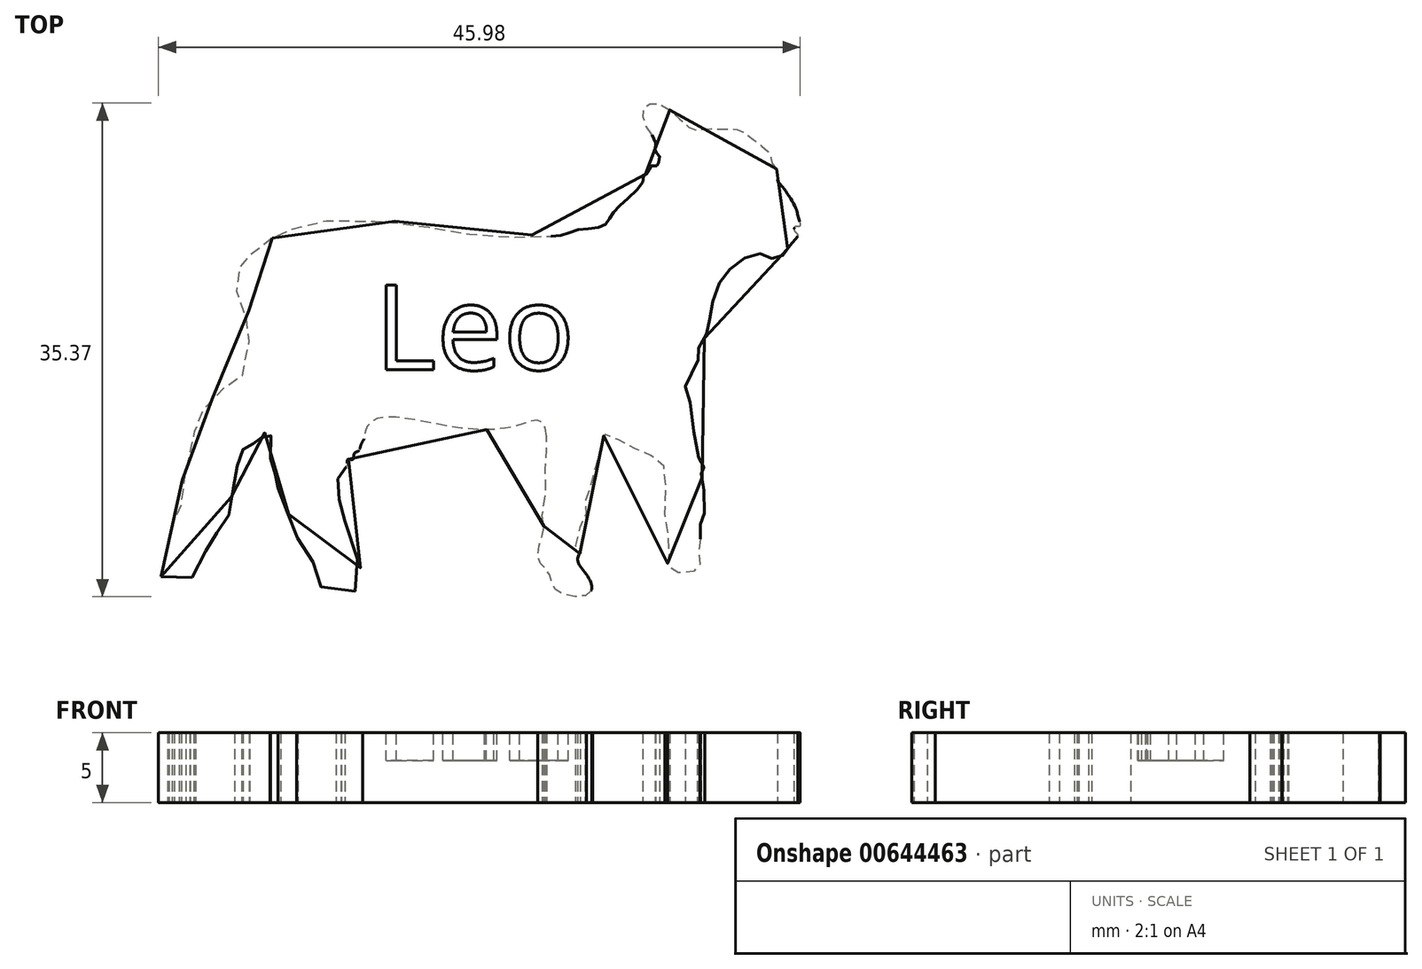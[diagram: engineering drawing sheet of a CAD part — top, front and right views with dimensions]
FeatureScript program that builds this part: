
annotation { "Feature Type Name" : "Feature", "Feature Type Description" : "" }
export const myFeature = defineFeature(function(context is Context, id is Id, definition is map)
    precondition{}
    {
        {
            var Q0;
            Q0=qCreatedBy(makeId("Top.planeOp"),FACE);
            var sketch = newSketch(context, id + "F0", { "sketchPlane" : qUnion([Q0])});
            skFitSpline(sketch, "E0", {"points": [v(-52.94, 10.3) * mm, v(-52.84, 11.68) * mm, v(-52.4, 12.88) * mm, v(-52.47, 13.1) * mm, v(-52, 13.63) * mm, v(-52.1, 13.85) * mm, v(-52.14, 14.2) * mm, v(-51.87, 14.8) * mm, v(-51.49, 15.13) * mm, v(-51.62, 15.97) * mm, v(-51.44, 17.15) * mm, v(-51.2, 17.9) * mm, v(-51.47, 18.15) * mm, v(-51.17, 18.5) * mm, v(-50.84, 19.3) * mm, v(-50.81, 20.13) * mm, v(-50.49, 20.45) * mm, v(-50.59, 21.16) * mm, v(-50.09, 21.6) * mm, v(-49.94, 22.2) * mm, v(-49.39, 22.7) * mm, v(-49.11, 23.4) * mm, v(-47.74, 24.2) * mm, v(-47.66, 24.51) * mm, v(-47.15, 24.58) * mm, v(-47.15, 25.06) * mm, v(-46.75, 25.6) * mm, v(-46.84, 27.96) * mm, v(-47.05, 28.11) * mm, v(-46.94, 28.45) * mm, v(-46.77, 28.93) * mm, v(-46.68, 29.98) * mm, v(-47.62, 30.87) * mm, v(-47.55, 31.93) * mm, v(-47.44, 32.43) * mm, v(-47.12, 32.54) * mm, v(-47.1, 33.02) * mm, v(-46.77, 33) * mm, v(-46.45, 33.46) * mm, v(-45.92, 33.69) * mm, v(-45.7, 34) * mm, v(-44.65, 34.61) * mm, v(-44.01, 34.57) * mm, v(-43.83, 35.09) * mm, v(-42.7, 35.16) * mm, v(-41.74, 35.67) * mm, v(-38.42, 35.76) * mm, v(-37.44, 35.7) * mm, v(-36.52, 35.51) * mm, v(-36.17, 35.76) * mm, v(-35.5, 35.27) * mm, v(-34.6, 35.28) * mm, v(-33.3, 35.28) * mm, v(-31.46, 34.9) * mm, v(-29.54, 34.73) * mm, v(-27.63, 34.62) * mm, v(-26.32, 34.77) * mm, v(-24.45, 34.7) * mm, v(-23.05, 35.14) * mm, v(-21.32, 35.39) * mm, v(-20.76, 36.04) * mm, v(-19.88, 37.05) * mm, v(-18.41, 38.61) * mm, v(-18.3, 39.1) * mm, v(-18, 39.24) * mm, v(-17.88, 39.7) * mm, v(-17.41, 39.73) * mm, v(-17.27, 40.02) * mm, v(-17.26, 40.52) * mm, v(-17.51, 40.66) * mm, v(-17.53, 41.39) * mm, v(-18.29, 42.78) * mm, v(-18.23, 44) * mm, v(-16.92, 44.02) * mm, v(-14.9, 42.35) * mm, v(-14.04, 42.37) * mm, v(-12.82, 42.35) * mm, v(-11.58, 42.3) * mm, v(-10.2, 41.37) * mm, v(-9.3, 40.5) * mm, v(-9.15, 39.85) * mm, v(-8.8, 39.41) * mm, v(-8.78, 38.78) * mm, v(-8.36, 38.13) * mm, v(-7.45, 36.64) * mm, v(-7.3, 36.08) * mm, v(-7.16, 35.56) * mm, v(-7.22, 35.37) * mm, v(-7.52, 35.36) * mm, v(-7.58, 35.12) * mm, v(-7.43, 34.92) * mm, v(-7.32, 34.67) * mm, v(-7.93, 33.96) * mm, v(-8.4, 33.3) * mm, v(-9.18, 33.08) * mm, v(-10.1, 33.43) * mm, v(-11.73, 32.7) * mm, v(-12.91, 31.37) * mm, v(-13.6, 29.17) * mm, v(-13.8, 27.78) * mm, v(-14.5, 26.47) * mm, v(-14.47, 25.6) * mm, v(-15.35, 24.22) * mm, v(-15.1, 23.05) * mm, v(-14.39, 18.7) * mm, v(-14.05, 18.12) * mm, v(-14.22, 17.82) * mm, v(-14.18, 17.4) * mm, v(-14.04, 14.66) * mm, v(-14.32, 14) * mm, v(-14.32, 12.55) * mm, v(-14.43, 11.53) * mm, v(-14.33, 11.07) * mm, v(-14.86, 10.65) * mm, v(-16.2, 10.65) * mm, v(-16.66, 11.18) * mm, v(-16.49, 12.1) * mm, v(-16.84, 14.86) * mm, v(-16.91, 18.19) * mm, v(-18.26, 19.14) * mm, v(-20.03, 20) * mm, v(-21.16, 20.45) * mm, v(-21.44, 19.07) * mm, v(-22.12, 17.34) * mm, v(-22.05, 16.7) * mm, v(-22.47, 16.35) * mm, v(-22.47, 15.04) * mm, v(-22.75, 14.26) * mm, v(-23.21, 12.42) * mm, v(-22.9, 12.1) * mm, v(-23.1, 11.57) * mm, v(-22.22, 10.04) * mm, v(-22.36, 9.02) * mm, v(-24.63, 9.3) * mm, v(-25.16, 10.58) * mm, v(-25.94, 11.6) * mm, v(-25.52, 13.73) * mm, v(-25.62, 14.5) * mm, v(-25.4, 16.13) * mm, v(-25.4, 17.55) * mm, v(-25.37, 18.47) * mm, v(-25.62, 21.34) * mm, v(-27.36, 21.13) * mm, v(-31.85, 20.99) * mm, v(-37.45, 21.62) * mm, v(-38.33, 20.67) * mm, v(-38.41, 20.12) * mm, v(-38.6, 19.78) * mm, v(-38.78, 19.3) * mm, v(-39.08, 19.14) * mm, v(-39.2, 18.7) * mm, v(-39.56, 18.68) * mm, v(-39.65, 18.18) * mm, v(-40.02, 17.9) * mm, v(-40.02, 17.46) * mm, v(-40.34, 17.23) * mm, v(-40.32, 16.47) * mm, v(-40.11, 15.65) * mm, v(-39.78, 14.77) * mm, v(-39.76, 14.04) * mm, v(-38.77, 11.2) * mm, v(-38.77, 9.43) * mm, v(-41.04, 9.17) * mm, v(-41.69, 10.15) * mm, v(-41.94, 11.17) * mm, v(-43.2, 12.65) * mm, v(-43.13, 13.24) * mm, v(-43.71, 14.64) * mm, v(-44.27, 15.43) * mm, v(-44.55, 16.64) * mm, v(-44.4, 16.95) * mm, v(-44.45, 17.28) * mm, v(-44.83, 17.67) * mm, v(-44.96, 18.08) * mm, v(-45.1, 18.7) * mm, v(-45.1, 18.93) * mm, v(-45.13, 19.94) * mm, v(-45.13, 20.64) * mm, v(-45.48, 20.63) * mm, v(-45.7, 20.33) * mm, v(-45.88, 20.15) * mm, v(-46.05, 20.09) * mm, v(-46.12, 19.95) * mm, v(-46.3, 19.9) * mm, v(-46.4, 19.69) * mm, v(-46.66, 19.57) * mm, v(-46.82, 19.43) * mm, v(-47.1, 19.4) * mm, v(-47.32, 19.1) * mm, v(-47.45, 18.5) * mm, v(-47.58, 17.65) * mm, v(-47.7, 16.87) * mm, v(-48, 15.55) * mm, v(-48.1, 14.61) * mm, v(-48.39, 14.04) * mm, v(-48.98, 13.39) * mm, v(-49.25, 12.6) * mm, v(-49.8, 12.05) * mm, v(-50.69, 10.46) * mm, v(-50.85, 10.07) * mm, v(-52.94, 10.3) * mm]});
            skSolve(sketch);
        }
        {
            var Q0;
            Q0=makeQuery(id+"F0.imprint","IMPRINT",FACE,{"disambiguationData":[TD([[makeQuery(id+"F0.imprint","IMPRINT",EDGE,{"derivedFrom":sQuery(id+"F0.wireOp",EDGE,"E0")}),-1.0]])]});
            extrude(context, id + "F1", {"entities" : qUnion([Q0]), "depth" : 5 * mm, "offsetDistance" : 25 * mm});
        }
        {
            var Q0;
            Q0=qCreatedBy(makeId("Top.planeOp"),FACE);
            var sketch = newSketch(context, id + "F2", { "sketchPlane" : qUnion([Q0])});
            skText(sketch, "E1", { "text": "Lamb", "fontName": "OpenSans-Regular.ttf"});
            const initialGuessF2  = {"E1": [-0.04163, 0.02566, 1, 0, 0.00606]};
            skSetInitialGuess(sketch, initialGuessF2);
            skSolve(sketch);
        }
        {
            var Q0;
            Q0 = qSketchRegion(id + "F2", true);
            extrude(context, id + "F3", {"entities" : qUnion([Q0]), "operationType" : NewBodyOperationType.REMOVE, "oppositeDirection" : true, "depth" : 1 * mm, "offsetDistance" : 25 * mm});
        }
        {
            var Q0;
            Q0=makeQuery(id+"F1.opExtrude","CAP_FACE",FACE,{"disambiguationData":[OSD([sQuery(id+"F0.wireOp",EDGE,"E0")])],"isStart":false});
            var sketch = newSketch(context, id + "F4", { "sketchPlane" : qUnion([Q0])});
            skText(sketch, "E2", { "text": "Leo", "fontName": "OpenSans-Regular.ttf"});
            const initialGuessF4  = {"E2": [-0.03764, 0.02511, 1, 0, 0.00613]};
            skSetInitialGuess(sketch, initialGuessF4);
            skSolve(sketch);
        }
        {
            var Q0;
            Q0 = qSketchRegion(id + "F4", true);
            extrude(context, id + "F5", {"entities" : qUnion([Q0]), "operationType" : NewBodyOperationType.REMOVE, "oppositeDirection" : true, "depth" : 2 * mm, "offsetDistance" : 25 * mm});
        }
        {
            var Q0;
            Q0=qCreatedBy(makeId("Top.planeOp"),FACE);
            var sketch = newSketch(context, id + "F6", { "sketchPlane" : qUnion([Q0])});
            skCircle(sketch, "E3", {"center": v(-12.72, 38.6) * mm, "radius": 0.95 * mm});
            skSolve(sketch);
        }
        {
            var Q0;
            Q0 = qSketchRegion(id + "F6", true);
            extrude(context, id + "F7", {"entities" : qUnion([Q0]), "operationType" : NewBodyOperationType.REMOVE, "oppositeDirection" : true, "depth" : 3 * mm, "offsetDistance" : 25 * mm});
        }
        {
            var Q0;
            {var subQ0=sQuery(id+"F0.wireOp",EDGE,"E0");Q0=makeQuery(id+"F5.boolean.opBoolean","SPLIT",FACE,{"disambiguationData":[TD([makeQuery(id+"F1.opExtrude","SWEPT_FACE",FACE,{"disambiguationData":[OSD([subQ0])]})])],"derivedFrom":makeQuery(id+"F1.opExtrude","CAP_FACE",FACE,{"disambiguationData":[OSD([subQ0])],"isStart":false})});}
            var sketch = newSketch(context, id + "F8", { "sketchPlane" : qUnion([Q0])});
            skCircle(sketch, "E4", {"center": v(-11.58, 39.5) * mm, "radius": 1.02 * mm});
            skSolve(sketch);
        }
        {
            var Q0;
            Q0=sQuery(id+"F8.wireOp",EDGE,"E4");
            extrude(context, id + "F9", {"bodyType" : ToolBodyType.SURFACE, "surfaceEntities" : qUnion([Q0]), "oppositeDirection" : true, "depth" : 5 * mm, "offsetDistance" : 25 * mm});
        }
    });
